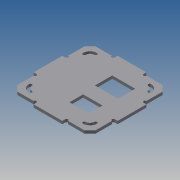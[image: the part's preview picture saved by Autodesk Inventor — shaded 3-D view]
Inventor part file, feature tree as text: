
AUTODESK INVENTOR PART (.ipt)
format: ipt  version: 2017 (Build 210142000, 142)  size: 168,960 bytes
history: native  units: mm
features: other x1, extrude x1, sketch x1
ambient origin geometry x8: Origin, YZ Plane, XZ Plane, XY Plane, X Axis, Y Axis, Z Axis, Center Point
bodies: Body1 (feature_tree)
feature tree (3):
  other  "Sólido1"
  extrude  "Extrusión1"  Depth=4.0mm
  sketch  "Boceto1"  dims[d0=40.0mm d1=4.0mm d2=2.0mm d3=109.0mm d4=117.0mm d5=4.0mm d6=8.0mm d10=24.0mm d11=32.0mm d12=31.0mm d13=71.0mm d14=3.0mm d15=20.0mm d16=19.0mm d17=27.0mm d19=24.0mm d20=4.0mm d21=0.0mm d22=2.1mm d23=8.0mm d24=75.0mm d25=75.0mm d26=109.0mm]
